# Revit family: 101010006208804
name_source: partatom
category: Modelos genéricos
revit_build: Autodesk Revit 2018 (Build: 20190510_1515(x64)
units: mm (PartAtom-declared; Revit-internal decimal feet)

## family parameters
Compartido = No
Corte con vacíos al cargar = No
Cota de conector redondo = Diámetro de uso
Puede alojar armadura = No
Punto de cálculo de habitación = No
Se basa en plano de trabajo = No
Siempre vertical = No
Tipo de pieza = Normal

## types (1)
- SEPARADORES TIPO TORRE 15 mm
    Aplicacion = Se aplican a modo de clip a presión en forma
horizontal sobre el encofrado o placa fenólica. (4 Un. x m2
Aprox.)
    Color = Negro
    Descripción = Torre de 20, para Fe de 8 a 12mm. Recubrimiento 20mm
    Dimension = 20 mm  [stored 0.0656168 ft]
    Empresa = CNP SPA.
    Espesor = 0 mm  [stored 0 ft]
    Material = PEAD
    Modelo = SEPARADORES TIPO TORRE
    Nombre SKU = SEPARADOR MOLDAJE TORRE 15MM BOLSA 2.000UN
    Num SKUs = 101010006208804
    URL = https://www.empresascnp.cl
    Unidad = Bolsa 1000 Un.
    Url Ficha tecnica = https://empresascnp.cl
    Uso = Para distanciar una barra o malla, del encofrado o fenólico.
    Ventajas = Mantiene la distancia en la altura exigida, mantiene los
espesores de piso o techos de hormigón requerido y son
más livianas.

note: [stored X ft] marks values corroborated as IEEE doubles in the binary element streams (Revit-internal decimal feet)

## geometry (parser evidence)
native form markers: Sweep x2
no freeform markers — native parametric forms only
